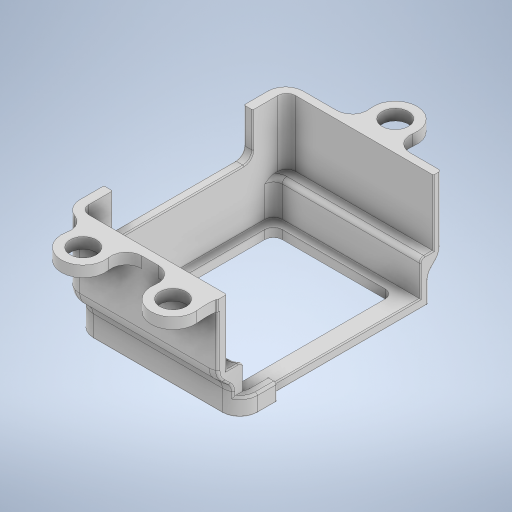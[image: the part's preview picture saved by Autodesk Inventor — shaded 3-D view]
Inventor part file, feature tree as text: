
AUTODESK INVENTOR PART (.ipt)
format: ipt  version: 2024 (Build 280153000, 153)  size: 814,080 bytes
history: native  units: in
note: dims shown in document units (in); Inventor stores cm internally (conversion verified against a paired STEP export)
features: extrude x8, fillet x8, chamfer x2, projected_geometry x2, plane x1
ambient origin geometry x8: Origin, YZ Plane, XZ Plane, XY Plane, X Axis, Y Axis, Z Axis, Center Point
bodies: Body1 (feature_tree)
feature tree (21):
  extrude  "Extrusion3"  Depth=0.0787in
  plane  "Work Plane1"
  extrude  "Extrusion4"  Depth=0.0787in
  extrude  "Extrusion7"  Depth=0.0787in TaperAngle=0.0deg
  extrude  "Extrusion8"  Depth=0.315in TaperAngle=0.0deg
  extrude  "Extrusion10"  Depth=0.315in
  extrude  "Extrusion11"  Depth=0.0787in TaperAngle=0.0deg
  extrude  "Extrusion12"  Depth=0.5906in TaperAngle=0.0deg
  extrude  "Extrusion13"  Depth=0.3937in
  chamfer  "Chamfer1"  Distance=0.2362in
  fillet  "Fillet1"  Radius=0.3937in
  fillet  "Fillet2"  Radius=0.2362in
  chamfer  "Chamfer2"  Distance=0.3937in
  fillet  "Fillet3"  Radius=0.8071in
  fillet  "Fillet4"  Radius=0.0984in
  fillet  "Fillet5"  Radius=0.1575in
  fillet  "Fillet6"  Radius=1.4646in
  fillet  "Fillet7"  Radius=1.0827in
  fillet  "Fillet8"  Radius=0.1575in
  projected_geometry  "Projected Loop3"
  projected_geometry  "Projected Loop4"
